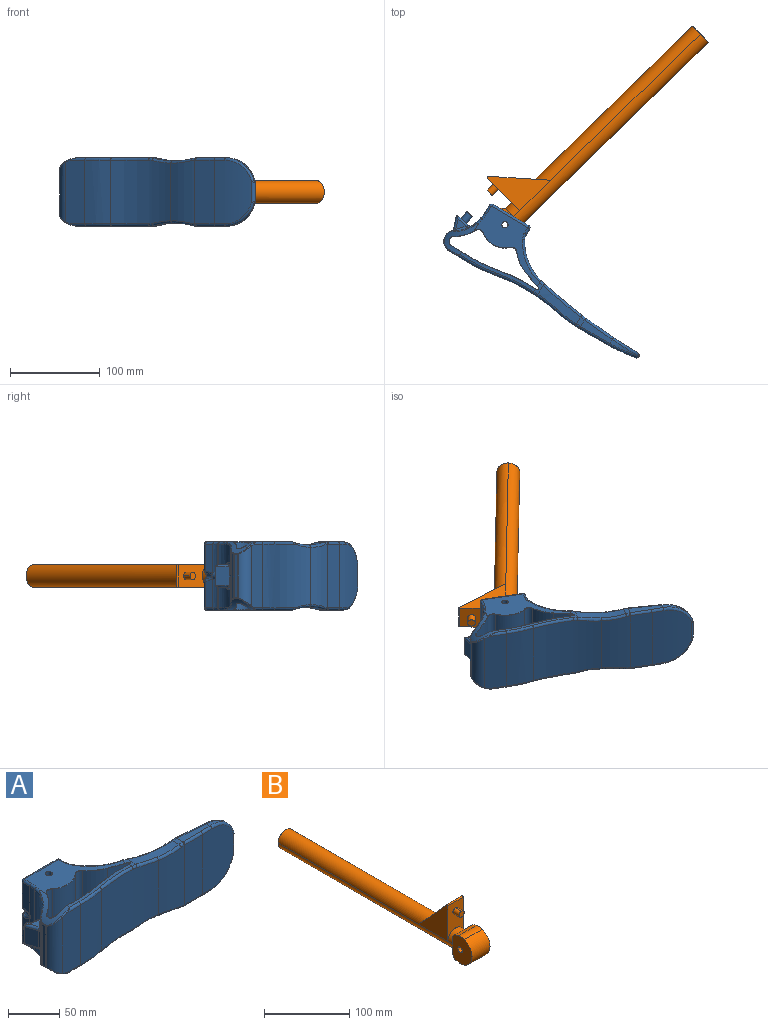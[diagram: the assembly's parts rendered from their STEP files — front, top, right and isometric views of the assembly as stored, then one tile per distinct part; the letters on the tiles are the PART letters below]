
ASSEMBLY  parts=2 mates=1
PART A: 230 faces, bbox 258.7x73.4x79.9 mm
  f0: plane 8.4x8.22mm, normal (0.17,0.98,0), area 54.5mm2, adj f11,f12
  f1: cylinder r=3.17mm len=10.25mm, axis (-0.36,-0.93,0), area 49.9mm2, adj f9,f15,f16,f18
  f2: bspline ~6.1x5.49mm, area 13.2mm2, adj f6,f7,f23,f24
  f3: bspline ~6.1x5.54mm, area 13.2mm2, adj f4,f5,f24,f25
  f4: cylinder r=36.83mm len=35.47mm, axis (0,1,0), area 128.2mm2, adj f3,f5,f25,f29,f31
  f5: bspline ~6.66x4mm, area 8.3mm2, adj f3,f4,f30,f31
  f6: cylinder r=36.83mm len=35.47mm, axis (0,1,0), area 128.8mm2, adj f2,f7,f23,f28,f36
  f7: bspline ~6.52x3.96mm, area 8.3mm2, adj f2,f6,f30,f36
  f8: sphere r=3.3mm, area 9.7mm2, adj f9,f18,f38
  f9: bspline ~11.34x4.79mm, area 26.7mm2, adj f1,f8,f15,f39
  f10: cylinder r=0.51mm len=20.32mm, axis (0,0,1), area 21.3mm2, adj f13,f14,f41,f45
  f11: cylinder r=4.17mm len=11.45mm, axis (0.17,0.98,0), area 133mm2, adj f0,f12,f45
  f12: cylinder r=4.17mm len=11.45mm, axis (0.17,0.98,0), area 133mm2, adj f0,f11,f45
  f13: bspline ~3.92x3.17mm, area 3mm2, adj f10,f46,f48
  f14: bspline ~3.59x3.55mm, area 3mm2, adj f10,f43,f49
  f15: bspline ~4.88x3.09mm, area 8.6mm2, adj f1,f9,f16,f52
  f16: bspline ~11.44x4.81mm, area 26.7mm2, adj f1,f15,f17,f53
  f17: sphere r=3.3mm, area 10.7mm2, adj f16,f18,f54
  f18: bspline ~12.36x8.25mm, area 47.7mm2, adj f1,f8,f17,f21,f55
  f19: cylinder r=2.54mm len=71.12mm, axis (0,0,1), area 283.8mm2, adj f37,f55,f56,f57
  f20: plane 33.02x12.7mm, normal (-1,0,0), area 419.4mm2, adj f22,f40,f55,f60
  f21: plane 35.62x15.3mm, normal (1,0,0), area 418.7mm2, adj f18,f22,f40,f55,f60
  f22: cylinder r=19.69mm len=39.37mm, axis (0,0,1), area 2042mm2, adj f20,f21,f40,f60
  f23: bspline ~35.21x26.69mm, area 172.4mm2, adj f2,f6,f27,f65
  f24: cylinder r=3.01mm len=24.64mm, axis (0,0,1), area 230.6mm2, adj f2,f3,f30,f65
  f25: bspline ~35.21x26.69mm, area 172.4mm2, adj f3,f4,f26,f65
  f26: torus R=302.26mm, axis (0,0,1), area 53.7mm2, adj f25,f29,f64,f65
  f27: torus R=302.26mm, axis (0,0,1), area 53.7mm2, adj f23,f28,f65,f66
  f28: plane 37.8x8.49mm, normal (0,0,-1), area 251.8mm2, adj f6,f27,f35,f63,f66
  f29: plane 37.8x8.49mm, normal (0,0,1), area 251.8mm2, adj f4,f26,f32,f64,f69
  f30: cylinder r=1.27mm len=28.33mm, axis (0,0,-1), area 6.1mm2, adj f5,f7,f24,f71
  f31: bspline ~35.98x29.26mm, area 169.7mm2, adj f4,f5,f32,f71
  f32: torus R=621.71mm, axis (0,0,1), area 150.9mm2, adj f29,f31,f33,f71
  f33: bspline ~5.75x3.16mm, area 21mm2, adj f32,f69,f70,f71
  f34: bspline ~5.7x3.16mm, area 21mm2, adj f35,f62,f63,f71
  f35: torus R=621.71mm, axis (0,0,1), area 150.9mm2, adj f28,f34,f36,f71
  f36: bspline ~35.87x28.83mm, area 169.7mm2, adj f6,f7,f35,f71
  f37: sphere r=2.54mm, area 7.6mm2, adj f19,f82,f83
  f38: cylinder r=3.3mm len=29.64mm, axis (0,0,1), area 153.7mm2, adj f8,f39,f55,f84
  f39: plane 33.43x9.7mm, normal (-1,0,0), area 290.6mm2, adj f9,f38,f52,f85
  f40: plane 39.38x32.45mm, normal (0,0,-1), area 1071.7mm2, adj f20,f21,f22,f55,f87,f88
  f41: plane 20.32x14.52mm, normal (-0.95,-0.31,0), area 310.8mm2, adj f10,f48,f49,f93
  f42: plane 11.82x10.15mm, normal (0,0,1), area 60.3mm2, adj f43,f49,f94
  f43: cylinder r=2.54mm len=17.68mm, axis (-0.98,0.17,0), area 58.9mm2, adj f14,f42,f45,f95
  f44: cylinder r=2.54mm len=12.7mm, axis (0,0,-1), area 40.7mm2, adj f45,f97,f98,f99
  f45: plane 20.32x17.24mm, normal (0.17,0.98,0), area 300.5mm2, adj f10,f11,f12,f43,f44,f46,f96,f100
  f46: cylinder r=2.54mm len=17.68mm, axis (0.98,-0.17,0), area 58.9mm2, adj f13,f45,f47,f101
  f47: plane 11.83x10.16mm, normal (0,0,-1), area 60.3mm2, adj f46,f48,f102
  f48: cylinder r=2.54mm len=15.32mm, axis (-0.31,0.95,0), area 52.3mm2, adj f13,f41,f47,f91,f103
  f49: cylinder r=2.54mm len=15.32mm, axis (0.31,-0.95,0), area 52.3mm2, adj f14,f41,f42,f92,f105
  f50: cylinder r=44.45mm len=75.72mm, axis (0,0,1), area 1913.9mm2, adj f51,f72,f77,f106
  f51: cylinder r=6.35mm len=75.72mm, axis (0,0,1), area 795.4mm2, adj f50,f61,f76,f107
  f52: cylinder r=24.77mm len=71.12mm, axis (0,0,1), area 499.1mm2, adj f15,f39,f53,f86,f104,f111
  f53: plane 33.75x10.02mm, normal (-1,0,0), area 290.6mm2, adj f16,f52,f54,f112
  f54: cylinder r=3.3mm len=29.64mm, axis (0,0,1), area 153.7mm2, adj f17,f53,f55,f113
  f55: plane 71.23x46.34mm, normal (0,1,0), area 1957.6mm2, adj f18,f19,f20,f21,f38,f40,f54,f60
  f56: plane 71.12x7.24mm, normal (1,0,0), area 514.9mm2, adj f19,f58,f82,f115
  f57: sphere r=2.54mm, area 7.6mm2, adj f19,f114,f115
  f58: cylinder r=12.7mm len=71.12mm, axis (0,0,1), area 435.2mm2, adj f56,f59,f81,f116
  f59: cylinder r=58.78mm len=71.12mm, axis (0,0,-1), area 3573mm2, adj f58,f71,f80,f117
  f60: plane 39.38x32.45mm, normal (0,0,1), area 1071.7mm2, adj f20,f21,f22,f55,f120,f121
  f61: cylinder r=26.04mm len=75.72mm, axis (0,0,1), area 2773.2mm2, adj f51,f75,f108,f123
  f62: bspline ~55.65x11.71mm, area 218.5mm2, adj f34,f71,f128,f129
  f63: cylinder r=25.4mm len=9.05mm, axis (0,1,0), area 47.4mm2, adj f28,f34,f67,f129,f133
  f64: cylinder r=2.54mm len=24.44mm, axis (-1,0,0), area 97.5mm2, adj f26,f29,f68,f134
  f65: cylinder r=304.8mm len=71.12mm, axis (0,0,1), area 2527.6mm2, adj f23,f24,f25,f26,f27,f134
  f66: cylinder r=2.54mm len=24.44mm, axis (-1,0,0), area 97.5mm2, adj f27,f28,f67,f134
  f67: bspline ~2.56x2.55mm, area 4.1mm2, adj f63,f66,f133,f134
  f68: bspline ~2.56x2.55mm, area 4.1mm2, adj f64,f69,f134,f135
  f69: cylinder r=25.4mm len=9.05mm, axis (0,-1,0), area 47.4mm2, adj f29,f33,f68,f135,f138
  f70: bspline ~55.1x11.64mm, area 218.5mm2, adj f33,f71,f138,f139
  f71: cylinder r=619.17mm len=134.12mm, axis (0,0,1), area 8960.4mm2, adj f30,f31,f32,f33,f34,f35,f36,f59
  f72: plane 75.83x20.95mm, normal (-0.33,-0.94,0), area 1671.9mm2, adj f50,f73,f78,f119,f126,f127,f140
  f73: cylinder r=1.27mm len=75.63mm, axis (0,0,1), area 268mm2, adj f72,f126,f141,f143
  f74: torus R=6.58mm, axis (0,0,1), area 4mm2, adj f75,f123,f124,f145
  f75: torus R=25.81mm, axis (0,0,1), area 13.1mm2, adj f61,f74,f76,f145
  f76: torus R=6.58mm, axis (0,0,1), area 3.8mm2, adj f51,f75,f77,f145
  f77: torus R=44.22mm, axis (0,0,1), area 9.1mm2, adj f50,f76,f78,f145
  f78: cylinder r=0.23mm len=18.77mm, axis (-0.94,0.33,0), area 7.1mm2, adj f72,f77,f140,f145
  f79: torus R=621.71mm, axis (0,0,1), area 2.8mm2, adj f71,f80,f139,f145
  f80: torus R=61.32mm, axis (0,0,-1), area 203.6mm2, adj f59,f79,f81,f145
  f81: torus R=15.24mm, axis (0,0,1), area 26.2mm2, adj f58,f80,f82,f145
  f82: cylinder r=2.54mm len=7.24mm, axis (0,1,0), area 28.9mm2, adj f37,f56,f81,f145
  f83: cylinder r=2.54mm len=46.23mm, axis (-1,0,0), area 184.4mm2, adj f37,f55,f84,f145
  f84: revolved ~3.3x3.3mm, area 14.9mm2, adj f38,f83,f85,f145
  f85: cylinder r=2.54mm len=9.4mm, axis (0,-1,0), area 37.5mm2, adj f39,f84,f86,f145
  f86: torus R=27.3mm, axis (0,0,1), area 29.3mm2, adj f52,f85,f89,f145
  f87: cylinder r=3.43mm len=21.59mm, axis (0,0,1), area 232.6mm2, adj f40,f88,f145
  f88: cylinder r=3.43mm len=21.59mm, axis (0,0,1), area 232.6mm2, adj f40,f87,f145
  f89: torus R=3.81mm, axis (0,0,1), area 3mm2, adj f86,f104,f145,f146
  f90: cylinder r=1.27mm len=60.9mm, axis (0,0,-1), area 27.5mm2, adj f148,f151,f152,f153
  f91: bspline ~4.97x3.71mm, area 9.1mm2, adj f48,f93,f103,f157
  f92: bspline ~5x3.76mm, area 9.1mm2, adj f49,f93,f105,f157
  f93: cylinder r=2.54mm len=20.32mm, axis (0,0,1), area 63.7mm2, adj f41,f91,f92,f157
  f94: torus R=35.56mm, axis (0,0,1), area 49mm2, adj f42,f95,f105,f158
  f95: bspline ~6.9x6.66mm, area 22.8mm2, adj f43,f94,f96,f158
  f96: cylinder r=2.54mm len=3.81mm, axis (0,0,-1), area 12.1mm2, adj f45,f95,f97,f158
  f97: plane 3.68x3.36mm, normal (0,0,1), area 0.2mm2, adj f44,f96,f98,f158
  f98: plane 12.7x1.98mm, normal (-0.88,0.47,0), area 28.4mm2, adj f44,f97,f99,f158
  f99: plane 3.68x3.36mm, normal (0,0,-1), area 0.2mm2, adj f44,f98,f100,f158
  f100: cylinder r=2.54mm len=3.81mm, axis (0,0,-1), area 12.1mm2, adj f45,f99,f101,f158
  f101: bspline ~6.9x6.66mm, area 22.8mm2, adj f46,f100,f102,f158
  f102: torus R=35.56mm, axis (0,0,1), area 49mm2, adj f47,f101,f103,f158
  f103: bspline ~4.68x4.48mm, area 11.9mm2, adj f48,f91,f102,f158
  f104: cylinder r=6.35mm len=71.12mm, axis (0,0,1), area 61.6mm2, adj f52,f89,f110,f158
  f105: bspline ~4.27x3.65mm, area 11.9mm2, adj f49,f92,f94,f158
  f106: torus R=44.2mm, axis (0,0,1), area 10.1mm2, adj f50,f107,f119,f160
  f107: torus R=6.6mm, axis (0,0,1), area 4.3mm2, adj f51,f106,f108,f160
  f108: torus R=25.78mm, axis (0,0,1), area 14.6mm2, adj f61,f107,f109,f160
  f109: torus R=6.6mm, axis (0,0,1), area 4.5mm2, adj f108,f122,f123,f160
  f110: torus R=3.81mm, axis (0,0,1), area 3mm2, adj f104,f111,f159,f160
  f111: torus R=27.3mm, axis (0,0,1), area 29.3mm2, adj f52,f110,f112,f160
  f112: cylinder r=2.54mm len=9.4mm, axis (0,1,0), area 37.5mm2, adj f53,f111,f113,f160
  f113: revolved ~3.3x3.3mm, area 14.9mm2, adj f54,f112,f114,f160
  f114: cylinder r=2.54mm len=46.23mm, axis (1,0,0), area 184.4mm2, adj f55,f57,f113,f160
  f115: cylinder r=2.54mm len=7.24mm, axis (0,1,0), area 28.9mm2, adj f56,f57,f116,f160
  f116: torus R=15.24mm, axis (0,0,1), area 26.2mm2, adj f58,f115,f117,f160
  f117: torus R=61.32mm, axis (0,0,-1), area 203.6mm2, adj f59,f116,f118,f160
  f118: torus R=621.71mm, axis (0,0,1), area 2.8mm2, adj f71,f117,f128,f160
  f119: cylinder r=0.25mm len=18.77mm, axis (0.94,-0.33,0), area 7.9mm2, adj f72,f106,f127,f160
  f120: cylinder r=3.43mm len=21.59mm, axis (0,0,1), area 232.6mm2, adj f60,f121,f160
  f121: cylinder r=3.43mm len=21.59mm, axis (0,0,1), area 232.6mm2, adj f60,f120,f160
  f122: torus R=44.2mm, axis (0,0,1), area 0.2mm2, adj f109,f160,f161,f162
  f123: cylinder r=6.35mm len=75.72mm, axis (0,0,1), area 841.6mm2, adj f61,f74,f109,f162
  f124: torus R=44.22mm, axis (0,0,1), area 0.2mm2, adj f74,f145,f150,f162
  f125: cylinder r=1.27mm len=60.9mm, axis (0,0,-1), area 27.5mm2, adj f149,f151,f164,f165
  f126: bspline ~3.14x1.71mm, area 1.6mm2, adj f72,f73,f127,f130,f169
  f127: bspline ~4.56x1.81mm, area 0.9mm2, adj f72,f119,f126,f169
  f128: bspline ~5.64x3.64mm, area 20.8mm2, adj f62,f71,f118,f169
  f129: cylinder r=127mm len=53.68mm, axis (0,1,0), area 565mm2, adj f62,f63,f132,f137,f169
  f130: bspline ~1.52x0.32mm, area 0.6mm2, adj f126,f143,f168,f169
  f131: bspline ~27.04x6.03mm, area 106.2mm2, adj f136,f138,f171,f213
  f132: bspline ~28.89x5.64mm, area 113.6mm2, adj f129,f133,f137,f172
  f133: bspline ~4.5x3.08mm, area 16.8mm2, adj f63,f67,f132,f172
  f134: plane 71.12x25.4mm, normal (0,-1,0), area 1806.4mm2, adj f64,f65,f66,f67,f68,f172
  f135: bspline ~4.5x3.04mm, area 16.8mm2, adj f68,f69,f136,f172
  f136: bspline ~28.89x5.64mm, area 113.6mm2, adj f131,f135,f138,f172
  f137: bspline ~27.3x6mm, area 106.2mm2, adj f129,f132,f173,f213
  f138: cylinder r=127mm len=53.68mm, axis (0,1,0), area 565mm2, adj f69,f70,f131,f136,f176
  f139: bspline ~5.64x3.64mm, area 20.8mm2, adj f70,f71,f79,f176
  f140: bspline ~2.24x0.97mm, area 0.8mm2, adj f72,f78,f141,f176
  f141: bspline ~3.07x1.6mm, area 1.4mm2, adj f73,f140,f142,f176
  f142: bspline ~1.52x0.29mm, area 0.5mm2, adj f141,f143,f176,f177
  f143: cylinder r=209.55mm len=75.72mm, axis (0,0,1), area 3807.2mm2, adj f73,f130,f142,f144,f168,f177
  f144: cylinder r=158.75mm len=75.72mm, axis (0,0,1), area 2328.4mm2, adj f143,f154,f167,f178
  f145: plane 92.09x50.96mm, normal (0,0,1), area 1852.2mm2, adj f74,f75,f76,f77,f78,f79,f80,f81
  f146: torus R=40.64mm, axis (0,0,1), area 41.3mm2, adj f89,f145,f158,f181
  f147: torus R=1.04mm, axis (0,-1,0), area 0mm2, adj f154,f179,f187,f188
  f148: bspline ~0.5x0.45mm, area 0.1mm2, adj f90,f189,f190
  f149: bspline ~0.5x0.45mm, area 0.1mm2, adj f125,f190,f191
  f150: bspline ~0.35x0.34mm, area 0.1mm2, adj f124,f162,f180,f193
  f151: plane 60.76x3.54mm, normal (1,0,0), area 215mm2, adj f90,f125,f190,f196
  f152: cylinder r=6.35mm len=68.49mm, axis (0,0,1), area 499.2mm2, adj f90,f154,f189,f197
  f153: bspline ~0.5x0.49mm, area 0.1mm2, adj f90,f196,f197
  f154: plane 75.73x25.42mm, normal (0,1,0), area 1888mm2, adj f144,f147,f152,f166,f170,f179,f188,f198
  f155: cylinder r=5.08mm len=49.28mm, axis (0,0,-1), area 72.3mm2, adj f156,f185,f195,f201
  f156: cylinder r=12.7mm len=51.35mm, axis (0,0,1), area 137.4mm2, adj f155,f157,f184,f202
  f157: cylinder r=6.35mm len=55.33mm, axis (0,0,-1), area 169.8mm2, adj f91,f92,f93,f156,f158,f183,f203
  f158: cylinder r=38.1mm len=71.12mm, axis (0,0,1), area 1717.4mm2, adj f94,f95,f96,f97,f98,f99,f100,f101
  f159: torus R=40.64mm, axis (0,0,1), area 41.2mm2, adj f110,f158,f160,f205
  f160: plane 92.04x50.88mm, normal (0,0,-1), area 1849.5mm2, adj f106,f107,f108,f109,f110,f111,f112,f113
  f161: bspline ~0.37x0.35mm, area 0.1mm2, adj f122,f162,f206,f207
  f162: cylinder r=44.45mm len=75.72mm, axis (0,0,1), area 1879.6mm2, adj f122,f123,f124,f150,f161,f163,f193,f207
  f163: cylinder r=1.27mm len=62.15mm, axis (0,0,1), area 49.9mm2, adj f162,f164,f192,f208
  f164: cylinder r=6.35mm len=61.21mm, axis (0,0,1), area 30.8mm2, adj f125,f163,f191,f209
  f165: bspline ~0.5x0.49mm, area 0.1mm2, adj f125,f196,f209
  f166: torus R=1.02mm, axis (0,1,0), area 0.1mm2, adj f154,f170,f198,f210
  f167: torus R=159mm, axis (0,0,1), area 12.3mm2, adj f144,f168,f170,f211
  f168: torus R=209.3mm, axis (0,0,1), area 19.4mm2, adj f130,f143,f167,f211
  f169: cylinder r=25.4mm len=12.6mm, axis (0,-1,0), area 55.6mm2, adj f126,f127,f128,f129,f130,f160,f173,f211
  f170: cylinder r=0.25mm len=12.95mm, axis (-1,0,0), area 5.2mm2, adj f154,f166,f167,f211
  f171: bspline ~5.52x3.1mm, area 20.8mm2, adj f131,f175,f176,f213
  f172: cylinder r=165.09mm len=71.08mm, axis (0,0,1), area 2211.1mm2, adj f132,f133,f134,f135,f136,f213
  f173: bspline ~5.52x3.1mm, area 20.8mm2, adj f137,f169,f174,f213
  f174: torus R=205.74mm, axis (0,0,1), area 190.1mm2, adj f173,f211,f212,f213
  f175: torus R=205.74mm, axis (0,0,1), area 190.1mm2, adj f171,f213,f214,f215
  f176: cylinder r=25.4mm len=12.6mm, axis (0,1,0), area 55.8mm2, adj f138,f139,f140,f141,f142,f145,f171,f215
  f177: torus R=209.32mm, axis (0,0,1), area 17.5mm2, adj f142,f143,f178,f215
  f178: torus R=158.98mm, axis (0,0,1), area 11.1mm2, adj f144,f177,f179,f215
  f179: cylinder r=0.23mm len=12.95mm, axis (-1,0,0), area 4.6mm2, adj f147,f154,f178,f215
  f180: cylinder r=1.27mm len=9.54mm, axis (0,-1,0), area 1.4mm2, adj f145,f150,f181,f217
  f181: bspline ~11.79x8.55mm, area 11.3mm2, adj f146,f180,f182,f217
  f182: bspline ~14.71x13.59mm, area 33.8mm2, adj f158,f181,f183,f217
  f183: bspline ~3.38x3.19mm, area 5.3mm2, adj f157,f182,f184,f217
  f184: bspline ~6.8x3mm, area 3mm2, adj f156,f183,f185,f217
  f185: bspline ~2.36x1.23mm, area 1.2mm2, adj f155,f184,f186,f217
  f186: cylinder r=1.27mm len=4.36mm, axis (0,1,0), area 4mm2, adj f185,f194,f195,f217
  f187: cylinder r=1.27mm len=3.58mm, axis (0,-1,0), area 0.5mm2, adj f147,f215,f216,f217
  f188: torus R=37.87mm, axis (0,1,0), area 4.7mm2, adj f147,f154,f189,f217
  f189: bspline ~6.91x5.85mm, area 3.8mm2, adj f148,f152,f188,f217
  f190: cylinder r=0.23mm len=4.04mm, axis (0,-1,0), area 1.9mm2, adj f148,f149,f151,f217
  f191: bspline ~3.13x1.56mm, area 0.3mm2, adj f149,f164,f192,f217
  f192: bspline ~1.19x1.19mm, area 0.4mm2, adj f163,f191,f193,f217
  f193: bspline ~21.88x19.8mm, area 10.9mm2, adj f150,f162,f192,f217
  f194: bspline ~2.36x1.23mm, area 1.2mm2, adj f186,f217,f218,f219
  f195: plane 48.92x4.36mm, normal (-1,0,0), area 213.1mm2, adj f155,f186,f200,f219
  f196: cylinder r=0.25mm len=4.05mm, axis (0,1,0), area 2.1mm2, adj f151,f153,f165,f221
  f197: bspline ~7.03x6.89mm, area 4.2mm2, adj f152,f153,f198,f221
  f198: torus R=37.85mm, axis (0,1,0), area 5.2mm2, adj f154,f166,f197,f221
  f199: bspline ~2.36x1.23mm, area 1.2mm2, adj f200,f219,f220,f221
  f200: cylinder r=1.27mm len=4.36mm, axis (0,-1,0), area 4mm2, adj f195,f199,f201,f221
  f201: bspline ~2.36x1.23mm, area 1.2mm2, adj f155,f200,f202,f221
  f202: bspline ~6.33x3mm, area 3mm2, adj f156,f201,f203,f221
  f203: bspline ~3.37x3.17mm, area 5.3mm2, adj f157,f202,f204,f221
  f204: bspline ~14.91x13.67mm, area 33.8mm2, adj f158,f203,f205,f221
  f205: bspline ~12.15x8.6mm, area 11.3mm2, adj f159,f204,f206,f221
  f206: cylinder r=1.27mm len=9.48mm, axis (0,1,0), area 1.4mm2, adj f160,f161,f205,f221
  f207: bspline ~25.61x23.59mm, area 12.1mm2, adj f161,f162,f208,f221
  f208: bspline ~1.23x1.22mm, area 0.5mm2, adj f163,f207,f209,f221
  f209: bspline ~3.01x1.41mm, area 0.4mm2, adj f164,f165,f208,f221
  f210: cylinder r=1.27mm len=3.56mm, axis (0,1,0), area 0.5mm2, adj f166,f211,f221,f222
  f211: plane 92.04x10.7mm, normal (0,0,-1), area 328.8mm2, adj f167,f168,f169,f170,f174,f210,f212,f223
  f212: torus R=162.56mm, axis (0,0,1), area 126.9mm2, adj f174,f211,f223,f224
  f213: cylinder r=203.2mm len=78.23mm, axis (0,0,1), area 5491.4mm2, adj f131,f137,f171,f172,f173,f174,f175,f224
  f214: torus R=162.56mm, axis (0,0,1), area 126.9mm2, adj f175,f215,f224,f225
  f215: plane 92.04x10.73mm, normal (0,0,1), area 331.2mm2, adj f175,f176,f177,f178,f179,f187,f214,f225
  f216: bspline ~7.94x3.04mm, area 8mm2, adj f187,f217,f225,f226
  f217: cylinder r=38.1mm len=42.35mm, axis (0,1,0), area 366.3mm2, adj f180,f181,f182,f183,f184,f185,f186,f187
  f218: bspline ~13.3x12.37mm, area 27mm2, adj f194,f217,f226,f227
  f219: cylinder r=5.08mm len=49.28mm, axis (0,0,1), area 72.3mm2, adj f194,f195,f199,f227
  f220: bspline ~13.3x12.92mm, area 26.8mm2, adj f199,f221,f227,f228
  f221: cylinder r=38.1mm len=42.35mm, axis (0,1,0), area 364.5mm2, adj f196,f197,f198,f199,f200,f201,f202,f203
  f222: bspline ~7.94x3.06mm, area 8mm2, adj f210,f221,f223,f228
  f223: cylinder r=2.54mm len=19.2mm, axis (-1,0,0), area 62.3mm2, adj f211,f212,f222,f229
  f224: cylinder r=165.1mm len=71.12mm, axis (0,0,1), area 2274.5mm2, adj f212,f213,f214,f229
  f225: cylinder r=2.54mm len=19.2mm, axis (-1,0,0), area 62.3mm2, adj f214,f215,f216,f229
  f226: torus R=36.83mm, axis (0,1,0), area 13.6mm2, adj f216,f217,f218,f229
  f227: cylinder r=12.7mm len=66.2mm, axis (0,0,1), area 939.2mm2, adj f218,f219,f220,f229
  f228: torus R=36.83mm, axis (0,1,0), area 13.6mm2, adj f220,f221,f222,f229
  f229: plane 71.12x25.4mm, normal (0,-1,0), area 1792.5mm2, adj f223,f224,f225,f226,f227,f228
PART B: 32 faces, bbox 29.9x324.4x71.3 mm
  f0: plane 8.43x8.4mm, normal (0,-1,0), area 55.2mm2, adj f8,f9
  f1: cylinder r=16mm len=29.85mm, axis (-1,0,0), area 297.2mm2, adj f2,f6,f10,f11
  f2: cylinder r=19.56mm len=37.31mm, axis (1,0,0), area 1485mm2, adj f1,f3,f10,f11
  f3: cylinder r=16mm len=29.85mm, axis (1,0,0), area 196.6mm2, adj f2,f7,f10,f11
  f4: cylinder r=3.81mm len=29.85mm, axis (1,0,0), area 357.2mm2, adj f5,f10,f11
  f5: cylinder r=3.81mm len=29.85mm, axis (1,0,0), area 357.2mm2, adj f4,f10,f11
  f6: plane 29.85x5.98mm, normal (0,0.26,0.97), area 184.9mm2, adj f1,f10,f11,f12
  f7: plane 29.85x6.93mm, normal (0,0.17,-0.98), area 210mm2, adj f3,f10,f11,f13
  f8: cylinder r=4.19mm len=10.16mm, axis (0,-1,0), area 133.8mm2, adj f0,f9,f15
  f9: cylinder r=4.19mm len=10.16mm, axis (0,-1,0), area 133.8mm2, adj f0,f8,f15
  f10: plane 38.96x32.34mm, normal (1,0,0), area 999.6mm2, adj f1,f2,f3,f4,f5,f6,f7,f12
  f11: plane 38.96x32.34mm, normal (-1,0,0), area 999.6mm2, adj f1,f2,f3,f4,f5,f6,f7,f12
  f12: plane 29.85x4.48mm, normal (0,0.76,0.65), area 175.9mm2, adj f6,f10,f11,f19,f20
  f13: plane 29.85x5.29mm, normal (0,0.81,-0.59), area 195mm2, adj f7,f10,f11,f19,f20
  f14: cylinder r=1.11mm len=25.4mm, axis (1,0,0), area 67.8mm2, adj f15,f17,f18,f22
  f15: plane 50.65x25.41mm, normal (0,-1,0), area 977.8mm2, adj f8,f9,f14,f18,f21,f22
  f16: plane 12.71x6.39mm, normal (0,-1,0), area 63.3mm2, adj f23,f25
  f17: plane 51.39x46.34mm, normal (0,0.74,0.67), area 1416.3mm2, adj f14,f18,f22,f27
  f18: plane 51.78x48.28mm, normal (1,0,0), area 1290.1mm2, adj f14,f15,f17,f28
  f19: plane 25.41x14.92mm, normal (0,1,0), area 125.7mm2, adj f10,f12,f13,f21,f28
  f20: plane 25.41x14.92mm, normal (0,1,0), area 125.7mm2, adj f11,f12,f13,f21,f28
  f21: cylinder r=12.7mm len=25.4mm, axis (0,1,0), area 405.4mm2, adj f15,f19,f20,f28
  f22: plane 51.78x48.28mm, normal (-1,0,0), area 1290.1mm2, adj f14,f15,f17,f28
  f23: plane 48.27x12.7mm, normal (0,0,-1), area 613mm2, adj f16,f26,f29
  f24: plane 12.78x12.71mm, normal (0,1,0), area 126.7mm2, adj f25,f29
  f25: cylinder r=6.35mm len=12.7mm, axis (0,1,0), area 202.7mm2, adj f16,f24,f29
  f26: plane 12.7x6.4mm, normal (0,0.74,0.67), area 85.3mm2, adj f23,f30
  f27: cylinder r=12.7mm len=245.13mm, axis (0,1,0), area 9614mm2, adj f17,f28,f31
  f28: cylinder r=12.7mm len=292.1mm, axis (0,1,0), area 11654.3mm2, adj f18,f19,f20,f21,f22,f27,f31
  f29: cylinder r=6.35mm len=292.1mm, axis (0,1,0), area 5827.1mm2, adj f23,f24,f25,f30,f31
  f30: cylinder r=6.35mm len=239.4mm, axis (0,1,0), area 4734.3mm2, adj f26,f29,f31
  f31: plane 25.44x25.4mm, normal (0,1,0), area 380mm2, adj f27,f28,f29,f30
PLACE A rot(axis=(0,0,-1),30.7deg) t=(-212.63,-232.53,64.43)mm fixed
PLACE B rot(axis=(-0.36,-0.86,-0.36),98.7deg) t=(-286.86,-195.85,102.53)mm
MATE revolute B.f2 <-> A.f22  axis (0,0,1) through (-286.86,-195.85,102.53)mm
